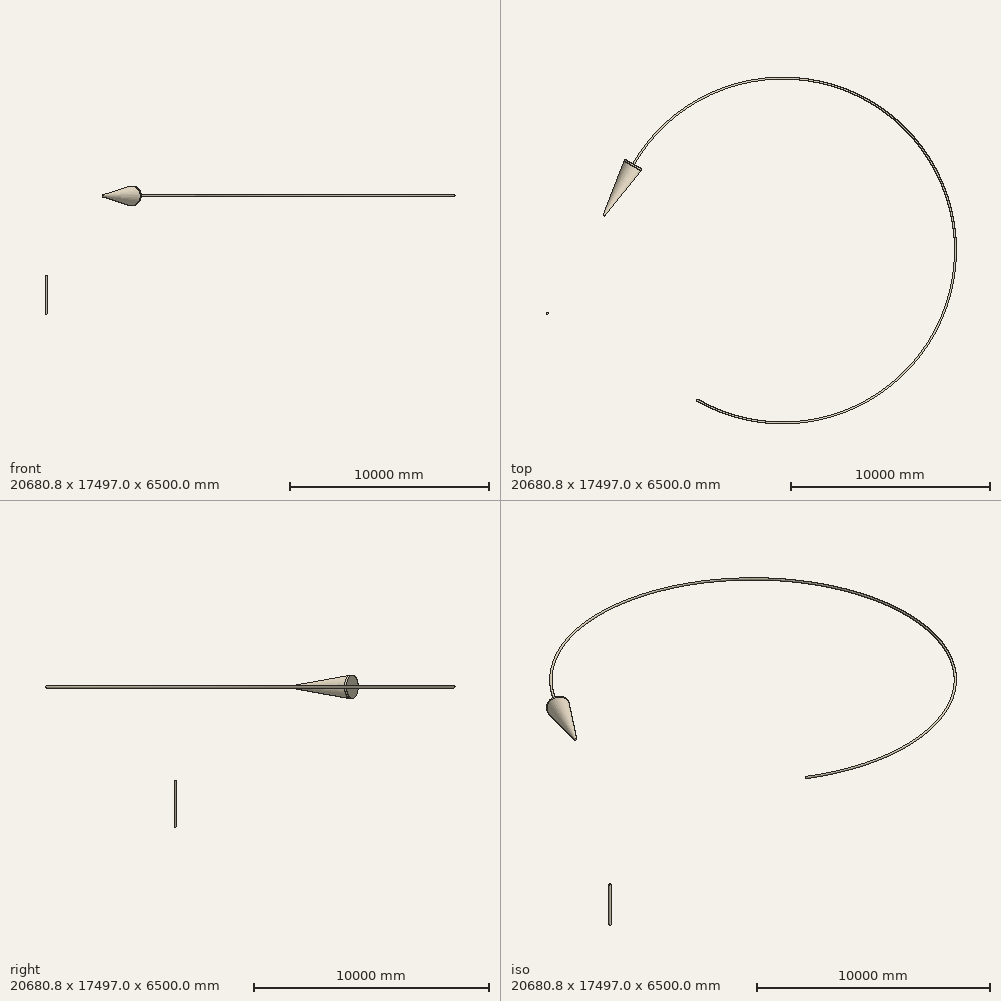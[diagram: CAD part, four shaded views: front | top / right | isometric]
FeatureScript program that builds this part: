
annotation { "Feature Type Name" : "Feature", "Feature Type Description" : "" }
export const myFeature = defineFeature(function(context is Context, id is Id, definition is map)
    precondition{}
    {
        {
            var Q0;
            Q0=qCreatedBy(makeId("Top.planeOp"),FACE);
            var sketch = newSketch(context, id + "F0", { "sketchPlane" : qUnion([Q0])});
            skArc(sketch, "E0", {"start": v(8698.48, 0) * mm, "mid": v(14849.24, 14849.24) * mm, "end": v(0, 8698.48) * mm});
            skSolve(sketch);
        }
        {
            var Q0;
            Q0=sQuery(id+"F0.wireOp",EDGE,"E0");
            var Q1;
            Q1=sQuery(id+"F0.wireOp",VERTEX,"E0.start");
            cPlane(context, id + "F1", {"entities" : qUnion([Q0, Q1]), "cplaneType" : CPlaneType.CURVE_POINT, "offset" : 25 * mm, "width" : 150 * mm, "height" : 150 * mm});
        }
        {
            var Q0;
            Q0=qCreatedBy(id+"F1.planeOp",FACE);
            var sketch = newSketch(context, id + "F2", { "sketchPlane" : qUnion([Q0])});
            skCircle(sketch, "E1", {"center": v(0, 0) * mm, "radius": 50 * mm});
            skSolve(sketch);
        }
        {
            var Q0;
            Q0=qSketchRegion(id+"F2",true);
            var Q1;
            Q1=sQuery(id+"F0.wireOp",EDGE,"E0");
            sweep(context, id + "F3", {"profiles" : qUnion([Q0]), "path" : qUnion([Q1])});
        }
        {
            var Q0;
            Q0=makeQuery(id+"F3.opSweep","CAP_FACE",FACE,{"disambiguationData":[OSD([sQuery(id+"F0.wireOp",VERTEX,"E0.end"),sQuery(id+"F2.wireOp",EDGE,"E1")])],"isStart":false});
            var sketch = newSketch(context, id + "F4", { "sketchPlane" : qUnion([Q0])});
            skCircle(sketch, "E2", {"center": v(0, 0) * mm, "radius": 500 * mm});
            skSolve(sketch);
        }
        {
            var Q0;
            Q0=qSketchRegion(id+"F4",true);
            extrude(context, id + "F5", {"entities" : qUnion([Q0]), "operationType" : NewBodyOperationType.ADD, "depth" : 3000 * mm, "offsetDistance" : 25 * mm});
        }
        {
            var Q0;
            Q0=makeQuery(id+"F5.opExtrude","CAP_EDGE",EDGE,{"disambiguationData":[OSD([sQuery(id+"F4.wireOp",EDGE,"E2")])],"isStart":false});
            chamfer(context, id + "F6", {"entities" : qUnion([Q0]), "chamferType" : ChamferType.TWO_OFFSETS, "width1" : 2900 * mm, "oppositeDirection" : true, "width2" : 450 * mm, "tangentPropagation" : true});
        }
        {
            var Q0;
            Q0=qCreatedBy(makeId("Top.planeOp"),FACE);
            var sketch = newSketch(context, id + "F7", { "sketchPlane" : qUnion([Q0])});
            skCircle(sketch, "E3", {"center": v(0, 0) * mm, "radius": 50 * mm});
            skSolve(sketch);
        }
        {
            var Q0;
            Q0=qSketchRegion(id+"F7",true);
            extrude(context, id + "F8", {"entities" : qUnion([Q0]), "oppositeDirection" : true, "depth" : 2000 * mm, "offsetDistance" : 25 * mm});
        }
        {
            var Q0;
            Q0=makeQuery(id+"F3.opSweep","SWEPT_BODY",BODY,{"disambiguationData":[OSD([sQuery(id+"F0.wireOp",EDGE,"E0"),sQuery(id+"F2.wireOp",EDGE,"E1")])]});
            var Q1;
            Q1=makeQuery(id+"F8.opExtrude","SWEPT_FACE",FACE,{"disambiguationData":[OSD([sQuery(id+"F7.wireOp",EDGE,"E3")])]});
            transform(context, id + "F9", {"entities" : qUnion([Q0]), "transformType" : TransformType.ROTATION, "transformAxis" : qUnion([Q1]), "angle" : 30 * degree, "oppositeDirection" : true, "makeCopy" : false});
        }
        {
            var Q0;
            Q0=makeQuery(id+"F3.opSweep","SWEPT_BODY",BODY,{"disambiguationData":[OSD([sQuery(id+"F0.wireOp",EDGE,"E0"),sQuery(id+"F2.wireOp",EDGE,"E1")])]});
            transform(context, id + "F10", {"entities" : qUnion([Q0]), "transformType" : TransformType.TRANSLATION_3D, "dx" : 0 * mm, "dy" : 0 * mm, "dz" : 4000 * mm, "makeCopy" : false});
        }
    });
